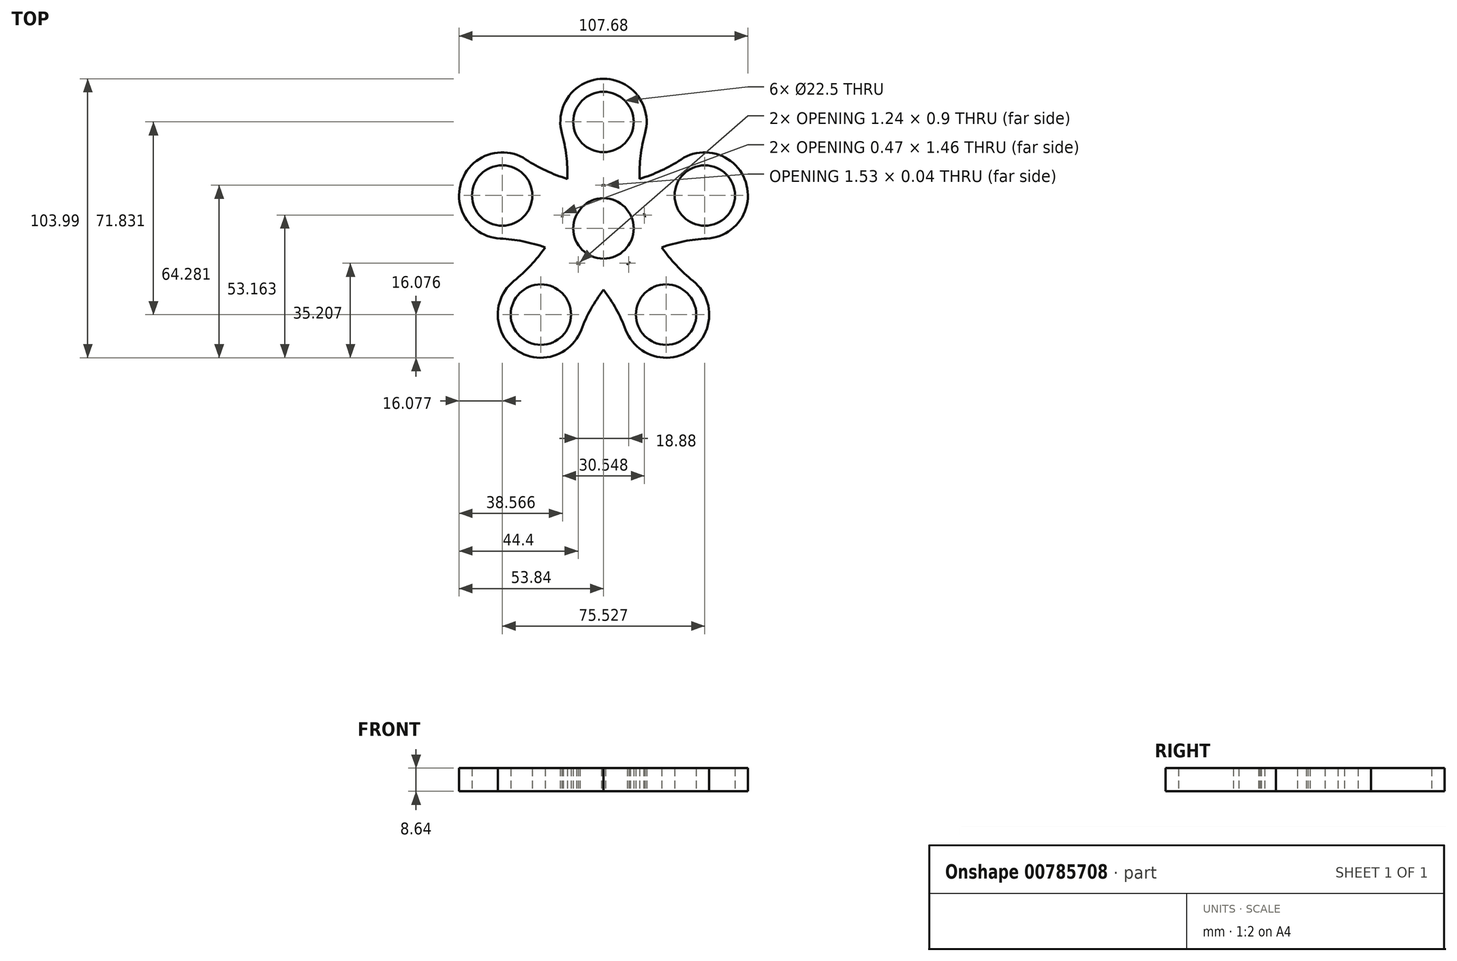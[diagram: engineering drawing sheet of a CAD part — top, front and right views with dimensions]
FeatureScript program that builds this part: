
annotation { "Feature Type Name" : "Feature", "Feature Type Description" : "" }
export const myFeature = defineFeature(function(context is Context, id is Id, definition is map)
    precondition{}
    {
        {
            var Q0;
            Q0=qCreatedBy(makeId("Top.planeOp"),FACE);
            var sketch = newSketch(context, id + "F0", { "sketchPlane" : qUnion([Q0])});
            skCircle(sketch, "E0", {"center": v(0, 0) * mm, "radius": 11.25 * mm});
            skCircle(sketch, "E1", {"center": v(0, 0) * mm, "radius": 16.08 * mm});
            skCircle(sketch, "E2", {"center": v(0, 39.7) * mm, "radius": 11.25 * mm});
            skCircle(sketch, "E3.1.0", {"center": v(-37.76, 12.27) * mm, "radius": 11.25 * mm});
            skCircle(sketch, "E3.2.0", {"center": v(-23.34, -32.12) * mm, "radius": 11.25 * mm});
            skCircle(sketch, "E3.3.0", {"center": v(23.34, -32.12) * mm, "radius": 11.25 * mm});
            skCircle(sketch, "E3.4.0", {"center": v(37.76, 12.27) * mm, "radius": 11.25 * mm});
            skCircle(sketch, "E4", {"center": v(37.76, 12.27) * mm, "radius": 16.08 * mm});
            skCircle(sketch, "E5", {"center": v(0, 39.7) * mm, "radius": 16.08 * mm});
            skCircle(sketch, "E6", {"center": v(-37.76, 12.27) * mm, "radius": 16.08 * mm});
            skCircle(sketch, "E7", {"center": v(-23.34, -32.12) * mm, "radius": 16.08 * mm});
            skCircle(sketch, "E8", {"center": v(23.34, -32.12) * mm, "radius": 16.08 * mm});
            skArc(sketch, "E9", {"start": v(-15.51, 4.23) * mm, "mid": v(-13.42, 19.85) * mm, "end": v(-15.51, 35.47) * mm});
            skArc(sketch, "E10", {"start": v(15.51, 35.47) * mm, "mid": v(13.42, 19.85) * mm, "end": v(15.51, 4.23) * mm});
            skArc(sketch, "E11.1.0", {"start": v(-28.94, 25.71) * mm, "mid": v(-14.74, 18.9) * mm, "end": v(0.77, 16.06) * mm});
            skArc(sketch, "E11.1.1", {"start": v(-8.82, -13.44) * mm, "mid": v(-23.03, -6.63) * mm, "end": v(-38.53, -3.79) * mm});
            skArc(sketch, "E11.2.0", {"start": v(-33.4, -19.58) * mm, "mid": v(-22.52, -8.18) * mm, "end": v(-15.04, 5.7) * mm});
            skArc(sketch, "E11.2.1", {"start": v(10.06, -12.54) * mm, "mid": v(-0.82, -23.95) * mm, "end": v(-8.3, -37.81) * mm});
            skArc(sketch, "E11.3.0", {"start": v(8.3, -37.81) * mm, "mid": v(0.82, -23.95) * mm, "end": v(-10.06, -12.54) * mm});
            skArc(sketch, "E11.3.1", {"start": v(15.04, 5.7) * mm, "mid": v(22.52, -8.18) * mm, "end": v(33.4, -19.58) * mm});
            skArc(sketch, "E11.4.0", {"start": v(38.53, -3.79) * mm, "mid": v(23.03, -6.63) * mm, "end": v(8.82, -13.44) * mm});
            skArc(sketch, "E11.4.1", {"start": v(-0.77, 16.06) * mm, "mid": v(14.74, 18.9) * mm, "end": v(28.94, 25.71) * mm});
            skSolve(sketch);
        }
        {
            var Q0;
            Q0=makeQuery(id+"F0.imprint","IMPRINT",FACE,{"disambiguationData":[TD([[makeQuery(id+"F0.imprint","IMPRINT",EDGE,{"derivedFrom":sQuery(id+"F0.wireOp",EDGE,"E0")}),-1.0]])]});
            var Q1;
            {var subQ0=sQuery(id+"F0.wireOp",EDGE,"E11.1.0");var subQ1=sQuery(id+"F0.wireOp",EDGE,"E1");var subQ2=makeQuery(id+"F0.imprint","INTERSECT",VERTEX,{"derivedFrom":[subQ1,subQ0]});Q1=makeQuery(id+"F0.imprint","IMPRINT",FACE,{"disambiguationData":[TD([[makeQuery(id+"F0.imprint","IMPRINT",EDGE,{"disambiguationData":[TD([[subQ2,1.0]])],"derivedFrom":subQ1}),-1.0]])]});}
            var Q2;
            {var subQ3=sQuery(id+"F0.wireOp",EDGE,"E10");var subQ6=sQuery(id+"F0.wireOp",EDGE,"E1");var subQ9=makeQuery(id+"F0.imprint","INTERSECT",VERTEX,{"derivedFrom":[subQ6,subQ3]});Q2=makeQuery(id+"F0.imprint","IMPRINT",FACE,{"disambiguationData":[TD([[makeQuery(id+"F0.imprint","IMPRINT",EDGE,{"disambiguationData":[TD([[subQ9,1.0]])],"derivedFrom":subQ6}),-1.0]])]});}
            var Q3;
            {var subQ0=sQuery(id+"F0.wireOp",EDGE,"E11.4.0");var subQ5=sQuery(id+"F0.wireOp",EDGE,"E4");var subQ6=makeQuery(id+"F0.imprint","INTERSECT",VERTEX,{"derivedFrom":[subQ5,subQ0]});Q3=makeQuery(id+"F0.imprint","IMPRINT",FACE,{"disambiguationData":[TD([[makeQuery(id+"F0.imprint","IMPRINT",EDGE,{"disambiguationData":[TD([[subQ6,1.0]])],"derivedFrom":subQ5}),-1.0]])]});}
            var Q4;
            Q4=makeQuery(id+"F0.imprint","IMPRINT",FACE,{"disambiguationData":[TD([[makeQuery(id+"F0.imprint","IMPRINT",EDGE,{"derivedFrom":sQuery(id+"F0.wireOp",EDGE,"E3.4.0")}),-1.0]])]});
            var Q5;
            {var subQ0=sQuery(id+"F0.wireOp",EDGE,"E11.3.0");var subQ6=sQuery(id+"F0.wireOp",EDGE,"E8");var subQ9=makeQuery(id+"F0.imprint","INTERSECT",VERTEX,{"derivedFrom":[subQ6,subQ0]});Q5=makeQuery(id+"F0.imprint","IMPRINT",FACE,{"disambiguationData":[TD([[makeQuery(id+"F0.imprint","IMPRINT",EDGE,{"disambiguationData":[TD([[subQ9,1.0]])],"derivedFrom":subQ6}),-1.0]])]});}
            var Q6;
            {var subQ5=sQuery(id+"F0.wireOp",EDGE,"E11.1.1");var subQ7=sQuery(id+"F0.wireOp",EDGE,"E1");var subQ8=makeQuery(id+"F0.imprint","INTERSECT",VERTEX,{"derivedFrom":[subQ7,subQ5]});Q6=makeQuery(id+"F0.imprint","IMPRINT",FACE,{"disambiguationData":[TD([[makeQuery(id+"F0.imprint","IMPRINT",EDGE,{"disambiguationData":[TD([[subQ8,-1.0]])],"derivedFrom":subQ7}),-1.0]])]});}
            var Q7;
            {var subQ0=sQuery(id+"F0.wireOp",EDGE,"E11.2.0");var subQ6=sQuery(id+"F0.wireOp",EDGE,"E7");var subQ9=makeQuery(id+"F0.imprint","INTERSECT",VERTEX,{"derivedFrom":[subQ6,subQ0]});Q7=makeQuery(id+"F0.imprint","IMPRINT",FACE,{"disambiguationData":[TD([[makeQuery(id+"F0.imprint","IMPRINT",EDGE,{"disambiguationData":[TD([[subQ9,1.0]])],"derivedFrom":subQ6}),-1.0]])]});}
            var Q8;
            Q8=makeQuery(id+"F0.imprint","IMPRINT",FACE,{"disambiguationData":[TD([[makeQuery(id+"F0.imprint","IMPRINT",EDGE,{"derivedFrom":sQuery(id+"F0.wireOp",EDGE,"E3.2.0")}),-1.0]])]});
            var Q9;
            {var subQ3=sQuery(id+"F0.wireOp",EDGE,"E9");var subQ5=sQuery(id+"F0.wireOp",EDGE,"E1");var subQ6=makeQuery(id+"F0.imprint","INTERSECT",VERTEX,{"derivedFrom":[subQ5,subQ3]});Q9=makeQuery(id+"F0.imprint","IMPRINT",FACE,{"disambiguationData":[TD([[makeQuery(id+"F0.imprint","IMPRINT",EDGE,{"disambiguationData":[TD([[subQ6,-1.0]])],"derivedFrom":subQ5}),-1.0]])]});}
            var Q10;
            Q10=makeQuery(id+"F0.imprint","IMPRINT",FACE,{"disambiguationData":[TD([[makeQuery(id+"F0.imprint","IMPRINT",EDGE,{"derivedFrom":sQuery(id+"F0.wireOp",EDGE,"E3.3.0")}),-1.0]])]});
            var Q11;
            Q11=makeQuery(id+"F0.imprint","IMPRINT",FACE,{"disambiguationData":[TD([[makeQuery(id+"F0.imprint","IMPRINT",EDGE,{"derivedFrom":sQuery(id+"F0.wireOp",EDGE,"E3.1.0")}),-1.0]])]});
            var Q12;
            {var subQ1=sQuery(id+"F0.wireOp",EDGE,"E6");var subQ5=sQuery(id+"F0.wireOp",EDGE,"E11.1.0");var subQ6=makeQuery(id+"F0.imprint","INTERSECT",VERTEX,{"derivedFrom":[subQ1,subQ5]});Q12=makeQuery(id+"F0.imprint","IMPRINT",FACE,{"disambiguationData":[TD([[makeQuery(id+"F0.imprint","IMPRINT",EDGE,{"disambiguationData":[TD([[subQ6,1.0]])],"derivedFrom":subQ1}),-1.0]])]});}
            var Q13;
            {var subQ0=sQuery(id+"F0.wireOp",EDGE,"E11.2.0");var subQ1=sQuery(id+"F0.wireOp",EDGE,"E1");var subQ2=makeQuery(id+"F0.imprint","INTERSECT",VERTEX,{"derivedFrom":[subQ1,subQ0]});Q13=makeQuery(id+"F0.imprint","IMPRINT",FACE,{"disambiguationData":[TD([[makeQuery(id+"F0.imprint","IMPRINT",EDGE,{"disambiguationData":[TD([[subQ2,1.0]])],"derivedFrom":subQ1}),-1.0]])]});}
            var Q14;
            {var subQ1=sQuery(id+"F0.wireOp",EDGE,"E5");var subQ5=sQuery(id+"F0.wireOp",EDGE,"E9");var subQ6=makeQuery(id+"F0.imprint","INTERSECT",VERTEX,{"derivedFrom":[subQ1,subQ5]});Q14=makeQuery(id+"F0.imprint","IMPRINT",FACE,{"disambiguationData":[TD([[makeQuery(id+"F0.imprint","IMPRINT",EDGE,{"disambiguationData":[TD([[subQ6,-1.0]])],"derivedFrom":subQ1}),-1.0]])]});}
            var Q15;
            Q15=makeQuery(id+"F0.imprint","IMPRINT",FACE,{"disambiguationData":[TD([[makeQuery(id+"F0.imprint","IMPRINT",EDGE,{"derivedFrom":sQuery(id+"F0.wireOp",EDGE,"E2")}),-1.0]])]});
            extrude(context, id + "F1", {"entities" : qUnion([Q0, Q1, Q2, Q3, Q4, Q5, Q6, Q7, Q8, Q9, Q10, Q11, Q12, Q13, Q14, Q15]), "depth" : 8.64 * mm, "offsetDistance" : 25.4 * mm});
        }
    });
